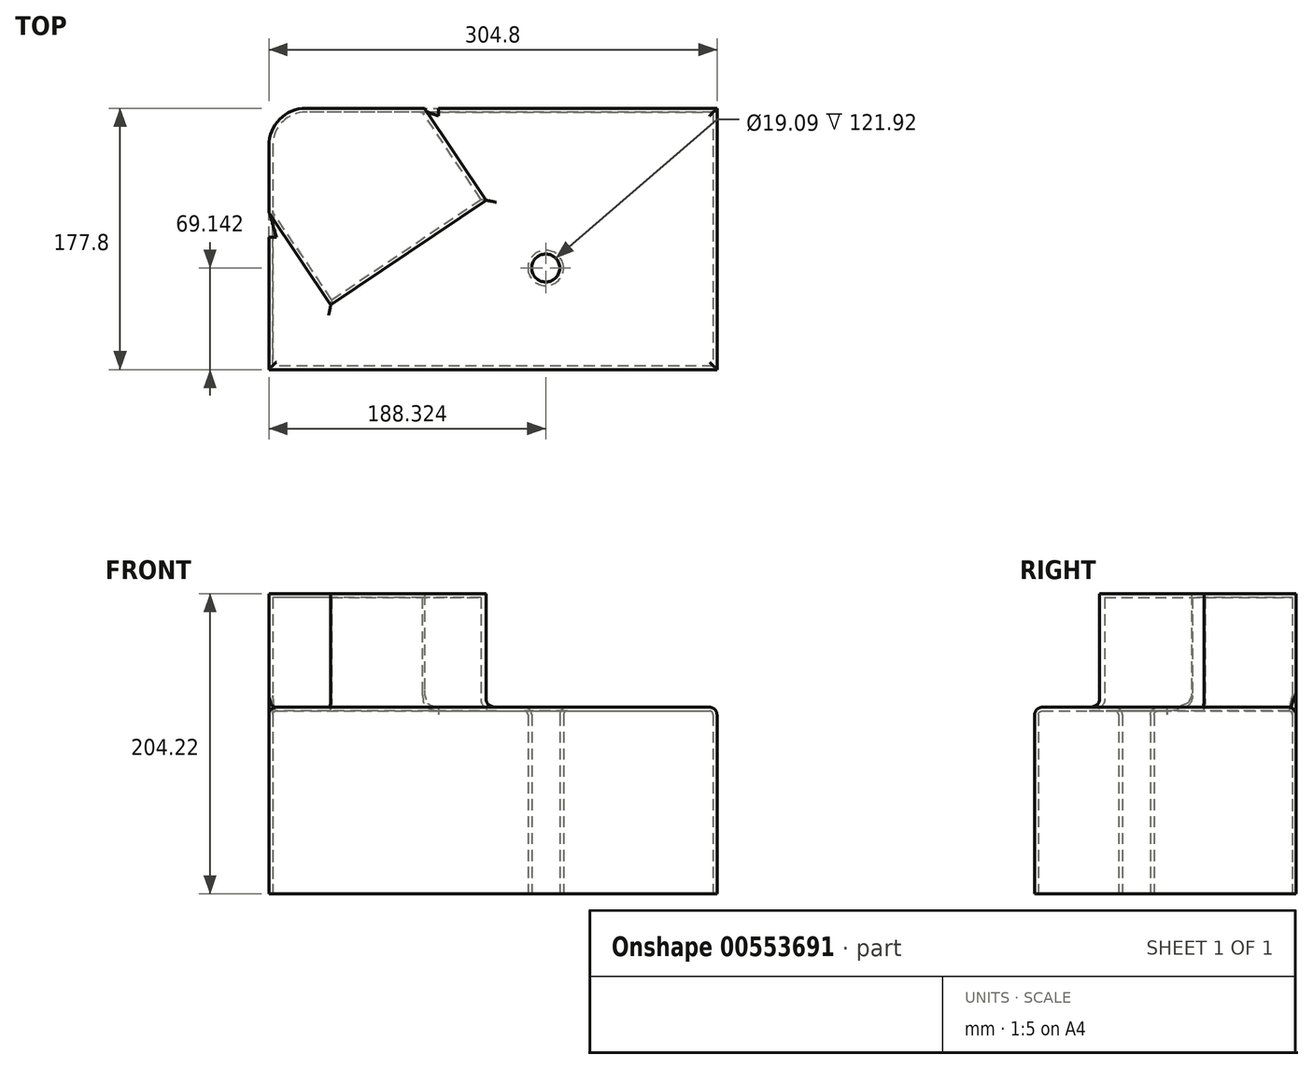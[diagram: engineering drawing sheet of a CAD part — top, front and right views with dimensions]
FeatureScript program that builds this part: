
annotation { "Feature Type Name" : "Feature", "Feature Type Description" : "" }
export const myFeature = defineFeature(function(context is Context, id is Id, definition is map)
    precondition{}
    {
        {
            var Q0;
            Q0=qCreatedBy(makeId("Top.planeOp"),FACE);
            var sketch = newSketch(context, id + "F0", { "sketchPlane" : qUnion([Q0])});
            skLineSegment(sketch, "E0.bottom", {"start": v(152.4, 88.9) * mm, "end": v(-152.4, 88.9) * mm});
            skLineSegment(sketch, "E0.top", {"start": v(152.4, -88.9) * mm, "end": v(-152.4, -88.9) * mm});
            skLineSegment(sketch, "E0.left", {"start": v(152.4, 88.9) * mm, "end": v(152.4, -88.9) * mm});
            skLineSegment(sketch, "E0.right", {"start": v(-152.4, 88.9) * mm, "end": v(-152.4, -88.9) * mm});
            skPoint(sketch, "E0.middle", {"position": v(0, 0) * mm});
            skCircle(sketch, "E1", {"center": v(35.92, -19.76) * mm, "radius": 9.55 * mm});
            skSolve(sketch);
        }
        {
            var Q0;
            Q0 = qSketchRegion(id + "F0", true);
            extrude(context, id + "F1", {"entities" : qUnion([Q0]), "depth" : 127 * mm, "offsetDistance" : 25.4 * mm});
        }
        {
            var Q0;
            Q0=makeQuery(id+"F1.opExtrude","CAP_FACE",FACE,{"disambiguationData":[OSD([sQuery(id+"F0.wireOp",EDGE,"E0.bottom"),sQuery(id+"F0.wireOp",EDGE,"E0.top"),sQuery(id+"F0.wireOp",EDGE,"E0.left"),sQuery(id+"F0.wireOp",EDGE,"E0.right"),sQuery(id+"F0.wireOp",EDGE,"E1")])],"isStart":false});
            var sketch = newSketch(context, id + "F2", { "sketchPlane" : qUnion([Q0])});
            skLineSegment(sketch, "E2", {"start": v(-152.4, 17.7) * mm, "end": v(-46.67, 88.9) * mm});
            skSolve(sketch);
        }
        {
            var Q0;
            Q0 = qSketchRegion(id + "F2", true);
            var Q1;
            {var subQ0=sQuery(id+"F2.wireOp",EDGE,"E2");Q1=makeQuery(id+"F2.imprint","IMPRINT",FACE,{"disambiguationData":[TD([[makeQuery(id+"F2.imprint","IMPRINT",EDGE,{"derivedFrom":subQ0}),1.0]])]});}
            extrude(context, id + "F3", {"entities" : qUnion([Q0, Q1]), "operationType" : NewBodyOperationType.ADD, "depth" : 77.22 * mm, "offsetDistance" : 25.4 * mm});
        }
        {
            var Q0;
            Q0=makeQuery(id+"F3.opExtrude","SWEPT_FACE",FACE,{"disambiguationData":[OSD([sQuery(id+"F2.wireOp",EDGE,"E2")])]});
            var sketch = newSketch(context, id + "F4", { "sketchPlane" : qUnion([Q0])});
            skLineSegment(sketch, "E3.0.0", {"start": v(-116.52, 127) * mm, "end": v(10.94, 127) * mm});
            skLineSegment(sketch, "E3.0.1", {"start": v(10.94, 127) * mm, "end": v(10.94, 204.22) * mm});
            skLineSegment(sketch, "E3.0.2", {"start": v(10.94, 204.22) * mm, "end": v(-116.52, 204.22) * mm});
            skLineSegment(sketch, "E3.0.3", {"start": v(-116.52, 204.22) * mm, "end": v(-116.52, 127) * mm});
            skSolve(sketch);
        }
        {
            var Q0;
            Q0 = qSketchRegion(id + "F4", true);
            extrude(context, id + "F5", {"entities" : qUnion([Q0]), "operationType" : NewBodyOperationType.ADD, "depth" : 75.44 * mm, "offsetDistance" : 25.4 * mm});
        }
        {
            var Q0;
            {var subQ0=sQuery(id+"F0.wireOp",EDGE,"E0.right");var subQ1=sQuery(id+"F0.wireOp",EDGE,"E0.bottom");Q0=makeQuery(id+"F3.boolean.opBoolean","MERGE",EDGE,{"derivedFrom":[makeQuery(id+"F1.opExtrude","SWEPT_EDGE",EDGE,{"disambiguationData":[OSD([subQ1,subQ0])]}),makeQuery(id+"F3.opExtrude","SWEPT_EDGE",EDGE,{"disambiguationData":[OSD([subQ1,subQ0])]})]});}
            fillet(context, id + "F6", {"entities" : qUnion([Q0]), "radius" : 25.4 * mm, "tangentPropagation" : true, "allowEdgeOverflow" : false});
        }
        {
            var Q0;
            Q0=makeQuery(id+"F1.opExtrude","CAP_FACE",FACE,{"disambiguationData":[OSD([sQuery(id+"F0.wireOp",EDGE,"E0.bottom"),sQuery(id+"F0.wireOp",EDGE,"E0.top"),sQuery(id+"F0.wireOp",EDGE,"E0.left"),sQuery(id+"F0.wireOp",EDGE,"E0.right"),sQuery(id+"F0.wireOp",EDGE,"E1")])],"isStart":false});
            fillet(context, id + "F7", {"entities" : qUnion([Q0]), "radius" : 5.08 * mm, "tangentPropagation" : true, "allowEdgeOverflow" : false});
        }
        {
            var Q0;
            Q0=makeQuery(id+"F1.opExtrude","CAP_FACE",FACE,{"disambiguationData":[OSD([sQuery(id+"F0.wireOp",EDGE,"E0.bottom"),sQuery(id+"F0.wireOp",EDGE,"E0.top"),sQuery(id+"F0.wireOp",EDGE,"E0.left"),sQuery(id+"F0.wireOp",EDGE,"E0.right"),sQuery(id+"F0.wireOp",EDGE,"E1")])],"isStart":true});
            shell(context, id + "F8", {"entities" : qUnion([Q0]), "thickness" : 2.54 * mm});
        }
    });
